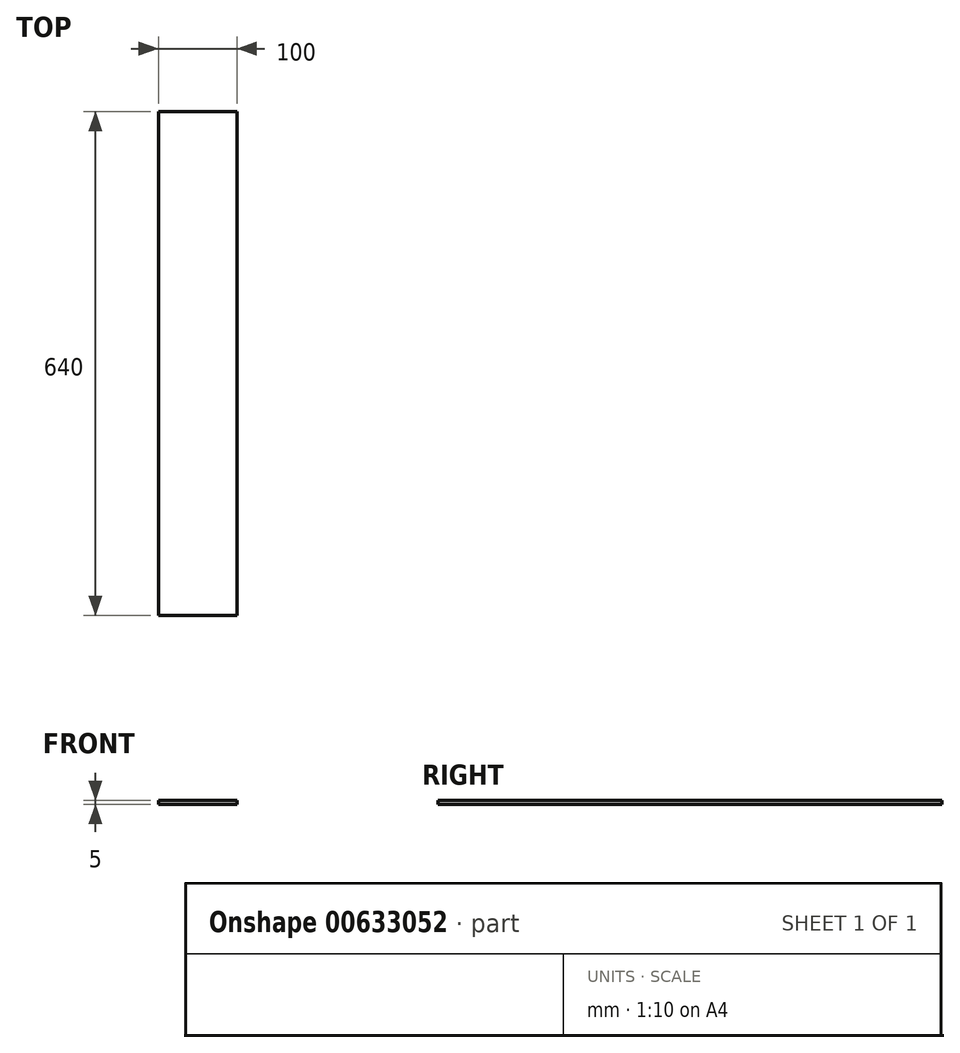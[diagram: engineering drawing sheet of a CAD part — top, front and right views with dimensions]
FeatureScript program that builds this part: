
annotation { "Feature Type Name" : "Feature", "Feature Type Description" : "" }
export const myFeature = defineFeature(function(context is Context, id is Id, definition is map)
    precondition{}
    {
        {
            var Q0;
            Q0=qCreatedBy(makeId("Front.planeOp"),FACE);
            var sketch = newSketch(context, id + "F0", { "sketchPlane" : qUnion([Q0])});
            skLineSegment(sketch, "E0.bottom", {"start": v(50, -2.5) * mm, "end": v(-50, -2.5) * mm});
            skLineSegment(sketch, "E0.top", {"start": v(50, 2.5) * mm, "end": v(-50, 2.5) * mm});
            skLineSegment(sketch, "E0.left", {"start": v(50, -2.5) * mm, "end": v(50, 2.5) * mm});
            skLineSegment(sketch, "E0.right", {"start": v(-50, -2.5) * mm, "end": v(-50, 2.5) * mm});
            skPoint(sketch, "E0.middle", {"position": v(0, 0) * mm});
            skSolve(sketch);
        }
        {
            var Q0;
            Q0=makeQuery(id+"F0.imprint","IMPRINT",FACE,{"disambiguationData":[TD([[makeQuery(id+"F0.imprint","IMPRINT",EDGE,{"derivedFrom":sQuery(id+"F0.wireOp",EDGE,"E0.bottom")}),-1.0]])]});
            extrude(context, id + "F1", {"entities" : qUnion([Q0]), "endBound" : BoundingType.SYMMETRIC, "depth" : 640 * mm, "offsetDistance" : 25 * mm});
        }
    });
